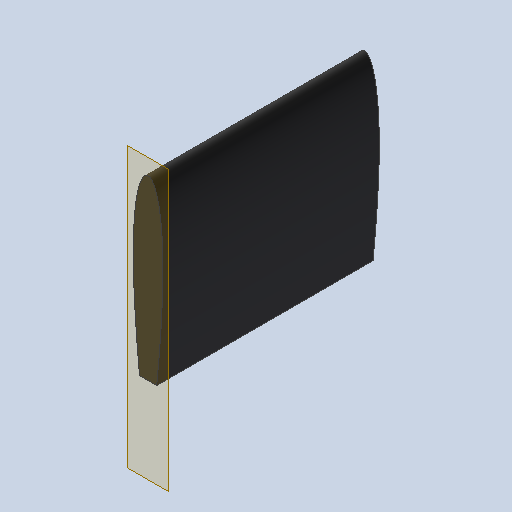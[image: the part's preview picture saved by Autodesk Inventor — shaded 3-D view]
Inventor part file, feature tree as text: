
AUTODESK INVENTOR PART (.ipt)
format: ipt  version: 2025.2 (Build 292293000, 293)  size: 120,832 bytes
history: native  units: in
note: dims shown in document units (in); Inventor stores cm internally (conversion verified against a paired STEP export)
features: other x3, sketch x1, plane x1
ambient origin geometry x8: Origin, YZ Plane, XZ Plane, XY Plane, X Axis, Y Axis, Z Axis, Center Point
bodies: Solid1 (feature_tree)
feature tree (5):
  other  "MiddleTailLeft.ipt"
  other  "Solid1::MiddleTailLeft.ipt"
  other  "TaggingFeature1"
  sketch  "Sketch1"  dims[d0=0.3937in]
  plane  "Work Plane1"
